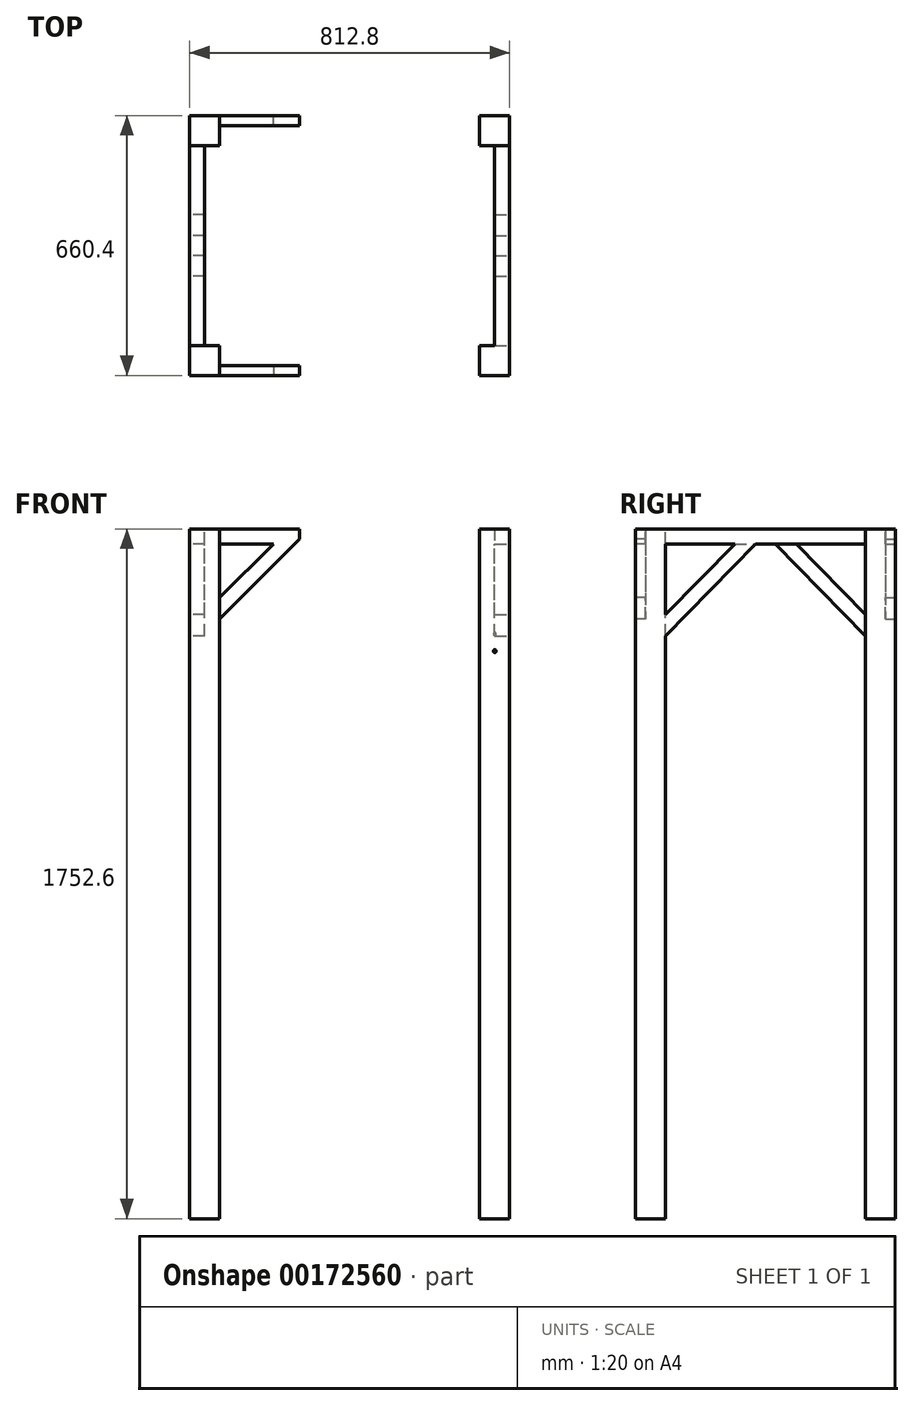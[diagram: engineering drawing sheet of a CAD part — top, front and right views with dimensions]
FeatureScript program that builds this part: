
annotation { "Feature Type Name" : "Feature", "Feature Type Description" : "" }
export const myFeature = defineFeature(function(context is Context, id is Id, definition is map)
    precondition{}
    {
        {
            var Q0;
            Q0=qCreatedBy(makeId("Front.planeOp"),FACE);
            var sketch = newSketch(context, id + "F0", { "sketchPlane" : qUnion([Q0])});
            skLineSegment(sketch, "E0", {"start": v(0, 0) * mm, "end": v(-330.2, 0) * mm, "construction": true});
            skLineSegment(sketch, "E1", {"start": v(0, 0) * mm, "end": v(330.2, 0) * mm, "construction": true});
            skLineSegment(sketch, "E2.bottom", {"start": v(-330.2, 0) * mm, "end": v(-406.4, 0) * mm});
            skLineSegment(sketch, "E2.top", {"start": v(-330.2, 1752.6) * mm, "end": v(-406.4, 1752.6) * mm});
            skLineSegment(sketch, "E2.left", {"start": v(-330.2, 0) * mm, "end": v(-330.2, 1752.6) * mm});
            skLineSegment(sketch, "E2.right", {"start": v(-406.4, 0) * mm, "end": v(-406.4, 1752.6) * mm});
            skLineSegment(sketch, "E3.bottom", {"start": v(330.2, 0) * mm, "end": v(406.4, 0) * mm});
            skLineSegment(sketch, "E3.top", {"start": v(330.2, 1752.6) * mm, "end": v(406.4, 1752.6) * mm});
            skLineSegment(sketch, "E3.left", {"start": v(330.2, 0) * mm, "end": v(330.2, 1752.6) * mm});
            skLineSegment(sketch, "E3.right", {"start": v(406.4, 0) * mm, "end": v(406.4, 1752.6) * mm});
            skSolve(sketch);
        }
        {
            var Q0;
            Q0=qCreatedBy(makeId("Right.planeOp"),FACE);
            var sketch = newSketch(context, id + "F1", { "sketchPlane" : qUnion([Q0])});
            skLineSegment(sketch, "E4", {"start": v(0, 0) * mm, "end": v(660.4, 0) * mm, "construction": true});
            skSolve(sketch);
        }
        {
            var Q0;
            Q0=qCreatedBy(makeId("Front.planeOp"),FACE);
            cPlane(context, id + "F2", {"entities" : qUnion([Q0]), "cplaneType" : CPlaneType.OFFSET, "offset" : 660.4 * mm, "oppositeDirection" : true, "width" : 152.4 * mm, "height" : 152.4 * mm});
        }
        {
            var Q0;
            Q0=qCreatedBy(id+"F2.planeOp",FACE);
            var sketch = newSketch(context, id + "F3", { "sketchPlane" : qUnion([Q0])});
            skLineSegment(sketch, "E5", {"start": v(0, 0) * mm, "end": v(330.2, 0) * mm, "construction": true});
            skLineSegment(sketch, "E6", {"start": v(0, 0) * mm, "end": v(-330.2, 0) * mm, "construction": true});
            skLineSegment(sketch, "E7.bottom", {"start": v(-330.2, 0) * mm, "end": v(-406.4, 0) * mm});
            skLineSegment(sketch, "E7.top", {"start": v(-330.2, 1752.6) * mm, "end": v(-406.4, 1752.6) * mm});
            skLineSegment(sketch, "E7.left", {"start": v(-330.2, 0) * mm, "end": v(-330.2, 1752.6) * mm});
            skLineSegment(sketch, "E7.right", {"start": v(-406.4, 0) * mm, "end": v(-406.4, 1752.6) * mm});
            skLineSegment(sketch, "E8.bottom", {"start": v(330.2, 0) * mm, "end": v(406.4, 0) * mm});
            skLineSegment(sketch, "E8.top", {"start": v(330.2, 1752.6) * mm, "end": v(406.4, 1752.6) * mm});
            skLineSegment(sketch, "E8.left", {"start": v(330.2, 0) * mm, "end": v(330.2, 1752.6) * mm});
            skLineSegment(sketch, "E8.right", {"start": v(406.4, 0) * mm, "end": v(406.4, 1752.6) * mm});
            skLineSegment(sketch, "E9", {"start": v(406.4, 0) * mm, "end": v(406.4, 990.6) * mm, "construction": true});
            skLineSegment(sketch, "E10", {"start": v(406.4, 990.6) * mm, "end": v(755.85, 990.6) * mm, "construction": true});
            skLineSegment(sketch, "E11", {"start": v(406.4, 0) * mm, "end": v(406.4, 1369.06) * mm, "construction": true});
            skLineSegment(sketch, "E12", {"start": v(406.4, 1369.06) * mm, "end": v(744.32, 1369.06) * mm, "construction": true});
            skSolve(sketch);
        }
        {
            var Q0;
            Q0 = qSketchRegion(id + "F3", true);
            extrude(context, id + "F4", {"entities" : qUnion([Q0]), "depth" : 76.2 * mm});
        }
        {
            var Q0;
            Q0 = qSketchRegion(id + "F1", true);
            var Q1;
            Q1 = qSketchRegion(id + "F0", true);
            extrude(context, id + "F5", {"entities" : qUnion([Q0, Q1]), "oppositeDirection" : true, "depth" : 76.2 * mm});
        }
        {
            var Q0;
            Q0 = qSketchRegion(id + "F0", true);
            extrude(context, id + "F6", {"entities" : qUnion([Q0]), "operationType" : NewBodyOperationType.ADD, "oppositeDirection" : true, "depth" : 25.4 * mm});
        }
        {
            var Q0;
            Q0 = qSketchRegion(id + "F3", true);
            extrude(context, id + "F7", {"entities" : qUnion([Q0]), "depth" : 25.4 * mm});
        }
        {
            var Q0;
            Q0=makeQuery(id+"F4.opExtrude","SWEPT_FACE",FACE,{"disambiguationData":[OSD([sQuery(id+"F3.wireOp",EDGE,"E8.right")])]});
            var sketch = newSketch(context, id + "F8", { "sketchPlane" : qUnion([Q0])});
            skLineSegment(sketch, "E13", {"start": v(584.2, 1752.6) * mm, "end": v(76.2, 1752.6) * mm});
            skLineSegment(sketch, "E14", {"start": v(584.2, 1714.5) * mm, "end": v(76.2, 1714.5) * mm});
            skLineSegment(sketch, "E15", {"start": v(76.2, 1752.6) * mm, "end": v(76.2, 1714.5) * mm});
            skLineSegment(sketch, "E16", {"start": v(584.2, 1752.6) * mm, "end": v(584.2, 1714.5) * mm});
            skSolve(sketch);
        }
        {
            var Q0;
            Q0 = qSketchRegion(id + "F8", true);
            extrude(context, id + "F9", {"entities" : qUnion([Q0]), "oppositeDirection" : true, "depth" : 38.1 * mm});
        }
        {
            var Q0;
            Q0=makeQuery(id+"F5.opExtrude","SWEPT_FACE",FACE,{"disambiguationData":[OSD([sQuery(id+"F0.wireOp",EDGE,"E2.right")])]});
            var sketch = newSketch(context, id + "F10", { "sketchPlane" : qUnion([Q0])});
            skLineSegment(sketch, "E17", {"start": v(-76.2, 1752.6) * mm, "end": v(-584.2, 1752.6) * mm});
            skLineSegment(sketch, "E18", {"start": v(-76.2, 1714.5) * mm, "end": v(-584.2, 1714.5) * mm});
            skLineSegment(sketch, "E19", {"start": v(-76.2, 1752.6) * mm, "end": v(-76.2, 1714.5) * mm});
            skLineSegment(sketch, "E20", {"start": v(-584.2, 1752.6) * mm, "end": v(-584.2, 1714.5) * mm});
            skSolve(sketch);
        }
        {
            var Q0;
            Q0 = qSketchRegion(id + "F10", true);
            extrude(context, id + "F11", {"entities" : qUnion([Q0]), "oppositeDirection" : true, "depth" : 38.1 * mm});
        }
        {
            var Q0;
            Q0=makeQuery(id+"F4.opExtrude","SWEPT_FACE",FACE,{"disambiguationData":[OSD([sQuery(id+"F3.wireOp",EDGE,"E7.right")])]});
            var sketch = newSketch(context, id + "F12", { "sketchPlane" : qUnion([Q0])});
            skLineSegment(sketch, "E21", {"start": v(-584.2, 1480.17) * mm, "end": v(-355.6, 1714.5) * mm});
            skLineSegment(sketch, "E22", {"start": v(-584.2, 1534.73) * mm, "end": v(-408.83, 1714.5) * mm});
            skLineSegment(sketch, "E23", {"start": v(-408.83, 1714.5) * mm, "end": v(-355.6, 1714.5) * mm});
            skLineSegment(sketch, "E24", {"start": v(-584.2, 1534.73) * mm, "end": v(-584.2, 1480.17) * mm});
            skSolve(sketch);
        }
        {
            var Q0;
            Q0 = qSketchRegion(id + "F12", true);
            extrude(context, id + "F13", {"entities" : qUnion([Q0]), "oppositeDirection" : true, "depth" : 38.1 * mm});
        }
        {
            var Q0;
            Q0=makeQuery(id+"F5.opExtrude","SWEPT_FACE",FACE,{"disambiguationData":[OSD([sQuery(id+"F0.wireOp",EDGE,"E2.right")])]});
            var sketch = newSketch(context, id + "F14", { "sketchPlane" : qUnion([Q0])});
            skLineSegment(sketch, "E25", {"start": v(-76.2, 1480.31) * mm, "end": v(-304.8, 1714.5) * mm});
            skLineSegment(sketch, "E26", {"start": v(-76.2, 1534.86) * mm, "end": v(-251.56, 1714.5) * mm});
            skLineSegment(sketch, "E27", {"start": v(-251.56, 1714.5) * mm, "end": v(-304.8, 1714.5) * mm});
            skLineSegment(sketch, "E28", {"start": v(-304.8, 1714.5) * mm, "end": v(-251.56, 1714.5) * mm});
            skLineSegment(sketch, "E29", {"start": v(-76.2, 1534.86) * mm, "end": v(-76.2, 1480.31) * mm});
            skSolve(sketch);
        }
        {
            var Q0;
            Q0 = qSketchRegion(id + "F14", true);
            extrude(context, id + "F15", {"entities" : qUnion([Q0]), "oppositeDirection" : true, "depth" : 25.4 * mm});
        }
        {
            var Q0;
            Q0=makeQuery(id+"F5.opExtrude","SWEPT_FACE",FACE,{"disambiguationData":[OSD([sQuery(id+"F0.wireOp",EDGE,"E3.right")])]});
            var sketch = newSketch(context, id + "F16", { "sketchPlane" : qUnion([Q0])});
            skLineSegment(sketch, "E30", {"start": v(76.2, 1480.31) * mm, "end": v(304.8, 1714.5) * mm});
            skLineSegment(sketch, "E31", {"start": v(76.2, 1534.86) * mm, "end": v(251.56, 1714.5) * mm});
            skLineSegment(sketch, "E32", {"start": v(251.56, 1714.5) * mm, "end": v(304.8, 1714.5) * mm});
            skLineSegment(sketch, "E33", {"start": v(76.2, 1480.31) * mm, "end": v(76.2, 1534.86) * mm});
            skSolve(sketch);
        }
        {
            var Q0;
            Q0 = qSketchRegion(id + "F16", true);
            extrude(context, id + "F17", {"entities" : qUnion([Q0]), "oppositeDirection" : true, "depth" : 38.1 * mm});
        }
        {
            var Q0;
            Q0=makeQuery(id+"F7.opExtrude","SWEPT_FACE",FACE,{"disambiguationData":[OSD([sQuery(id+"F3.wireOp",EDGE,"E8.right")])]});
            var sketch = newSketch(context, id + "F18", { "sketchPlane" : qUnion([Q0])});
            skLineSegment(sketch, "E34", {"start": v(584.2, 1480.31) * mm, "end": v(355.6, 1714.5) * mm});
            skLineSegment(sketch, "E35", {"start": v(408.84, 1714.5) * mm, "end": v(584.2, 1534.86) * mm});
            skLineSegment(sketch, "E36", {"start": v(355.6, 1714.5) * mm, "end": v(408.84, 1714.5) * mm});
            skLineSegment(sketch, "E37", {"start": v(584.2, 1534.86) * mm, "end": v(584.2, 1480.31) * mm});
            skSolve(sketch);
        }
        {
            var Q0;
            Q0=makeQuery(id+"F4.opExtrude","CAP_FACE",FACE,{"disambiguationData":[OSD([sQuery(id+"F3.wireOp",EDGE,"E7.bottom"),sQuery(id+"F3.wireOp",EDGE,"E7.top"),sQuery(id+"F3.wireOp",EDGE,"E7.left"),sQuery(id+"F3.wireOp",EDGE,"E7.right"),sQuery(id+"F3.wireOp",EDGE,"E8.bottom"),sQuery(id+"F3.wireOp",EDGE,"E8.top"),sQuery(id+"F3.wireOp",EDGE,"E8.left"),sQuery(id+"F3.wireOp",EDGE,"E8.right"),sQuery(id+"F3.wireOp",EDGE,"7tmQgZbe-lUGM-ekjJ-V75s-b2bH1PlLNMDt"),sQuery(id+"F3.wireOp",EDGE,"9oeJorli-9Kxg-f2F7-JcsI-I3q3USsDNPX7"),sQuery(id+"F3.wireOp",EDGE,"25wDnhQm-lPVD-gHgN-B71o-P6sYls9N5KOy"),sQuery(id+"F3.wireOp",EDGE,"il2duZ0r-kvnG-iQqj-aWlA-yyv6otPGMYP1")])],"isStart":true});
            var sketch = newSketch(context, id + "F19", { "sketchPlane" : qUnion([Q0])});
            skLineSegment(sketch, "E38", {"start": v(-330.2, 1752.6) * mm, "end": v(-127, 1752.6) * mm});
            skLineSegment(sketch, "E39", {"start": v(-127, 1727.2) * mm, "end": v(-330.2, 1524) * mm});
            skLineSegment(sketch, "E40", {"start": v(330.2, 1752.6) * mm, "end": v(127, 1752.6) * mm});
            skLineSegment(sketch, "E41", {"start": v(127, 1727.2) * mm, "end": v(330.2, 1524) * mm});
            skLineSegment(sketch, "E42", {"start": v(-127, 1752.6) * mm, "end": v(-127, 1727.2) * mm});
            skLineSegment(sketch, "E43", {"start": v(127, 1752.6) * mm, "end": v(127, 1727.2) * mm});
            skPoint(sketch, "E44.orphan", {"position": v(-101.6, 1752.6) * mm});
            skPoint(sketch, "E45.orphan", {"position": v(101.6, 1752.6) * mm});
            skLineSegment(sketch, "E46", {"start": v(-139.7, 1714.5) * mm, "end": v(-330.2, 1714.5) * mm});
            skLineSegment(sketch, "E47", {"start": v(-193.58, 1714.5) * mm, "end": v(-330.2, 1577.88) * mm});
            skLineSegment(sketch, "E48", {"start": v(139.7, 1714.5) * mm, "end": v(330.2, 1714.5) * mm});
            skLineSegment(sketch, "E49", {"start": v(193.58, 1714.5) * mm, "end": v(330.2, 1577.88) * mm});
            skSolve(sketch);
        }
        {
            var Q0;
            {var subQ4=sQuery(id+"F14.wireOp",EDGE,"E26");Q0=makeQuery(id+"F14.imprint","IMPRINT",FACE,{"disambiguationData":[TD([[makeQuery(id+"F14.imprint","IMPRINT",EDGE,{"derivedFrom":subQ4}),1.0]])]});}
            extrude(context, id + "F20", {"entities" : qUnion([Q0]), "oppositeDirection" : true, "depth" : 38.1 * mm});
        }
        {
            var Q0;
            Q0 = qSketchRegion(id + "F16", true);
            extrude(context, id + "F21", {"entities" : qUnion([Q0]), "operationType" : NewBodyOperationType.ADD, "oppositeDirection" : true, "depth" : 25.4 * mm});
        }
        {
            var Q0;
            Q0 = qSketchRegion(id + "F18", true);
            extrude(context, id + "F22", {"entities" : qUnion([Q0]), "oppositeDirection" : true, "depth" : 38.1 * mm});
        }
        {
            var Q0;
            {var subQ0=sQuery(id+"F19.wireOp",EDGE,"E38");Q0=makeQuery(id+"F19.imprint","IMPRINT",FACE,{"disambiguationData":[TD([[makeQuery(id+"F19.imprint","IMPRINT",EDGE,{"derivedFrom":subQ0}),-1.0]])]});}
            var Q1;
            {var subQ0=sQuery(id+"F19.wireOp",EDGE,"E40");Q1=makeQuery(id+"F19.imprint","IMPRINT",FACE,{"disambiguationData":[TD([[makeQuery(id+"F19.imprint","IMPRINT",EDGE,{"derivedFrom":subQ0}),1.0]])]});}
            var Q2;
            {var subQ5=sQuery(id+"F19.wireOp",EDGE,"E47");Q2=makeQuery(id+"F19.imprint","IMPRINT",FACE,{"disambiguationData":[TD([[makeQuery(id+"F19.imprint","IMPRINT",EDGE,{"derivedFrom":subQ5}),1.0]])]});}
            var Q3;
            {var subQ5=sQuery(id+"F19.wireOp",EDGE,"E49");Q3=makeQuery(id+"F19.imprint","IMPRINT",FACE,{"disambiguationData":[TD([[makeQuery(id+"F19.imprint","IMPRINT",EDGE,{"derivedFrom":subQ5}),-1.0]])]});}
            extrude(context, id + "F23", {"entities" : qUnion([Q0, Q1, Q2, Q3]), "oppositeDirection" : true, "depth" : 25.4 * mm});
        }
        {
            var Q0;
            Q0=makeQuery(id+"F4.opExtrude","CAP_FACE",FACE,{"disambiguationData":[OSD([sQuery(id+"F3.wireOp",EDGE,"E7.bottom"),sQuery(id+"F3.wireOp",EDGE,"E7.top"),sQuery(id+"F3.wireOp",EDGE,"E7.left"),sQuery(id+"F3.wireOp",EDGE,"E7.right"),sQuery(id+"F3.wireOp",EDGE,"E8.bottom"),sQuery(id+"F3.wireOp",EDGE,"E8.top"),sQuery(id+"F3.wireOp",EDGE,"E8.left"),sQuery(id+"F3.wireOp",EDGE,"E8.right"),sQuery(id+"F3.wireOp",EDGE,"7tmQgZbe-lUGM-ekjJ-V75s-b2bH1PlLNMDt"),sQuery(id+"F3.wireOp",EDGE,"9oeJorli-9Kxg-f2F7-JcsI-I3q3USsDNPX7"),sQuery(id+"F3.wireOp",EDGE,"25wDnhQm-lPVD-gHgN-B71o-P6sYls9N5KOy"),sQuery(id+"F3.wireOp",EDGE,"il2duZ0r-kvnG-iQqj-aWlA-yyv6otPGMYP1")])],"isStart":true});
            var sketch = newSketch(context, id + "F24", { "sketchPlane" : qUnion([Q0])});
            skLineSegment(sketch, "E50", {"start": v(-330.2, 1524) * mm, "end": v(-406.4, 1524) * mm, "construction": true});
            skLineSegment(sketch, "E51", {"start": v(-368.3, 1524) * mm, "end": v(-368.3, 1485.9) * mm, "construction": true});
            skCircle(sketch, "E52", {"center": v(-368.3, 1485.9) * mm, "radius": 3.5 * mm});
            skSolve(sketch);
        }
        {
            var Q0;
            Q0 = qSketchRegion(id + "F24", true);
            extrude(context, id + "F25", {"entities" : qUnion([Q0]), "operationType" : NewBodyOperationType.REMOVE, "oppositeDirection" : true, "depth" : 1.27 * mm});
        }
        {
            var Q0;
            Q0=makeQuery(id+"F5.opExtrude","CAP_FACE",FACE,{"disambiguationData":[OSD([sQuery(id+"F0.wireOp",EDGE,"E2.bottom"),sQuery(id+"F0.wireOp",EDGE,"E2.top"),sQuery(id+"F0.wireOp",EDGE,"E2.left"),sQuery(id+"F0.wireOp",EDGE,"E2.right"),sQuery(id+"F0.wireOp",EDGE,"E3.bottom"),sQuery(id+"F0.wireOp",EDGE,"E3.top"),sQuery(id+"F0.wireOp",EDGE,"E3.left"),sQuery(id+"F0.wireOp",EDGE,"E3.right"),sQuery(id+"F0.wireOp",EDGE,"vTQmmdSK-y7x3-ExHp-8qoF-U8qnrNzBsml3"),sQuery(id+"F0.wireOp",EDGE,"SaCECFoh-iSPG-4jtW-FqOt-tgZXtXGdQvM0"),sQuery(id+"F0.wireOp",EDGE,"d3jEO5Kd-dWc0-ZTVm-38Kg-CgUppXvorKHE"),sQuery(id+"F0.wireOp",EDGE,"EGGj8675-JTCR-3Mwa-YaGc-P4h6rzPofOSH")])],"isStart":true});
            var sketch = newSketch(context, id + "F26", { "sketchPlane" : qUnion([Q0])});
            skLineSegment(sketch, "E53", {"start": v(330.2, 1480.17) * mm, "end": v(406.4, 1480.17) * mm, "construction": true});
            skLineSegment(sketch, "E54", {"start": v(368.3, 1480.17) * mm, "end": v(368.3, 1442.07) * mm, "construction": true});
            skCircle(sketch, "E55", {"center": v(368.3, 1442.07) * mm, "radius": 3.5 * mm});
            skSolve(sketch);
        }
        {
            var Q0;
            Q0 = qSketchRegion(id + "F26", true);
            extrude(context, id + "F27", {"entities" : qUnion([Q0]), "operationType" : NewBodyOperationType.REMOVE, "oppositeDirection" : true, "depth" : 1.27 * mm});
        }
        {
            var Q0;
            Q0=qCreatedBy(makeId("Front.planeOp"),FACE);
            cPlane(context, id + "F28", {"entities" : qUnion([Q0]), "cplaneType" : CPlaneType.OFFSET, "offset" : 330.2 * mm, "oppositeDirection" : true, "width" : 152.4 * mm, "height" : 152.4 * mm});
        }
        {
            var Q0;
            Q0=makeQuery(id+"F23.opExtrude","SWEPT_BODY",BODY,{"disambiguationData":[OSD([sQuery(id+"F3.wireOp",EDGE,"E8.left"),sQuery(id+"F19.wireOp",EDGE,"E38"),sQuery(id+"F19.wireOp",EDGE,"E39"),sQuery(id+"F19.wireOp",EDGE,"E42"),sQuery(id+"F19.wireOp",EDGE,"E46"),sQuery(id+"F19.wireOp",EDGE,"E47")])]});
            var Q1;
            Q1=makeQuery(id+"F23.opExtrude","SWEPT_BODY",BODY,{"disambiguationData":[OSD([sQuery(id+"F3.wireOp",EDGE,"E7.left"),sQuery(id+"F19.wireOp",EDGE,"E40"),sQuery(id+"F19.wireOp",EDGE,"E41"),sQuery(id+"F19.wireOp",EDGE,"E43"),sQuery(id+"F19.wireOp",EDGE,"E48"),sQuery(id+"F19.wireOp",EDGE,"E49")])]});
            var Q2;
            Q2=qCreatedBy(id+"F28.planeOp",FACE);
            mirror(context, id + "F29", {"entities" : qUnion([Q0, Q1]), "mirrorPlane" : qUnion([Q2])});
        }
        {
            var Q0;
            Q0=makeQuery(id+"F7.opExtrude","SWEPT_BODY",BODY,{"disambiguationData":[OSD([sQuery(id+"F3.wireOp",EDGE,"E7.bottom"),sQuery(id+"F3.wireOp",EDGE,"E7.top"),sQuery(id+"F3.wireOp",EDGE,"E7.left"),sQuery(id+"F3.wireOp",EDGE,"E7.right")])]});
            deleteBodies(context, id + "F30", {"entities" : qUnion([Q0])});
        }
        {
            var Q0;
            Q0=makeQuery(id+"F7.opExtrude","SWEPT_BODY",BODY,{"disambiguationData":[OSD([sQuery(id+"F3.wireOp",EDGE,"E8.bottom"),sQuery(id+"F3.wireOp",EDGE,"E8.top"),sQuery(id+"F3.wireOp",EDGE,"E8.left"),sQuery(id+"F3.wireOp",EDGE,"E8.right")])]});
            deleteBodies(context, id + "F31", {"entities" : qUnion([Q0])});
        }
        {
            var Q0;
            Q0=makeQuery(id+"F15.opExtrude","SWEPT_BODY",BODY,{"disambiguationData":[OSD([sQuery(id+"F14.wireOp",EDGE,"E25"),sQuery(id+"F14.wireOp",EDGE,"E26"),sQuery(id+"F14.wireOp",EDGE,"E28"),sQuery(id+"F14.wireOp",EDGE,"E29")])]});
            deleteBodies(context, id + "F32", {"entities" : qUnion([Q0])});
        }
    });
